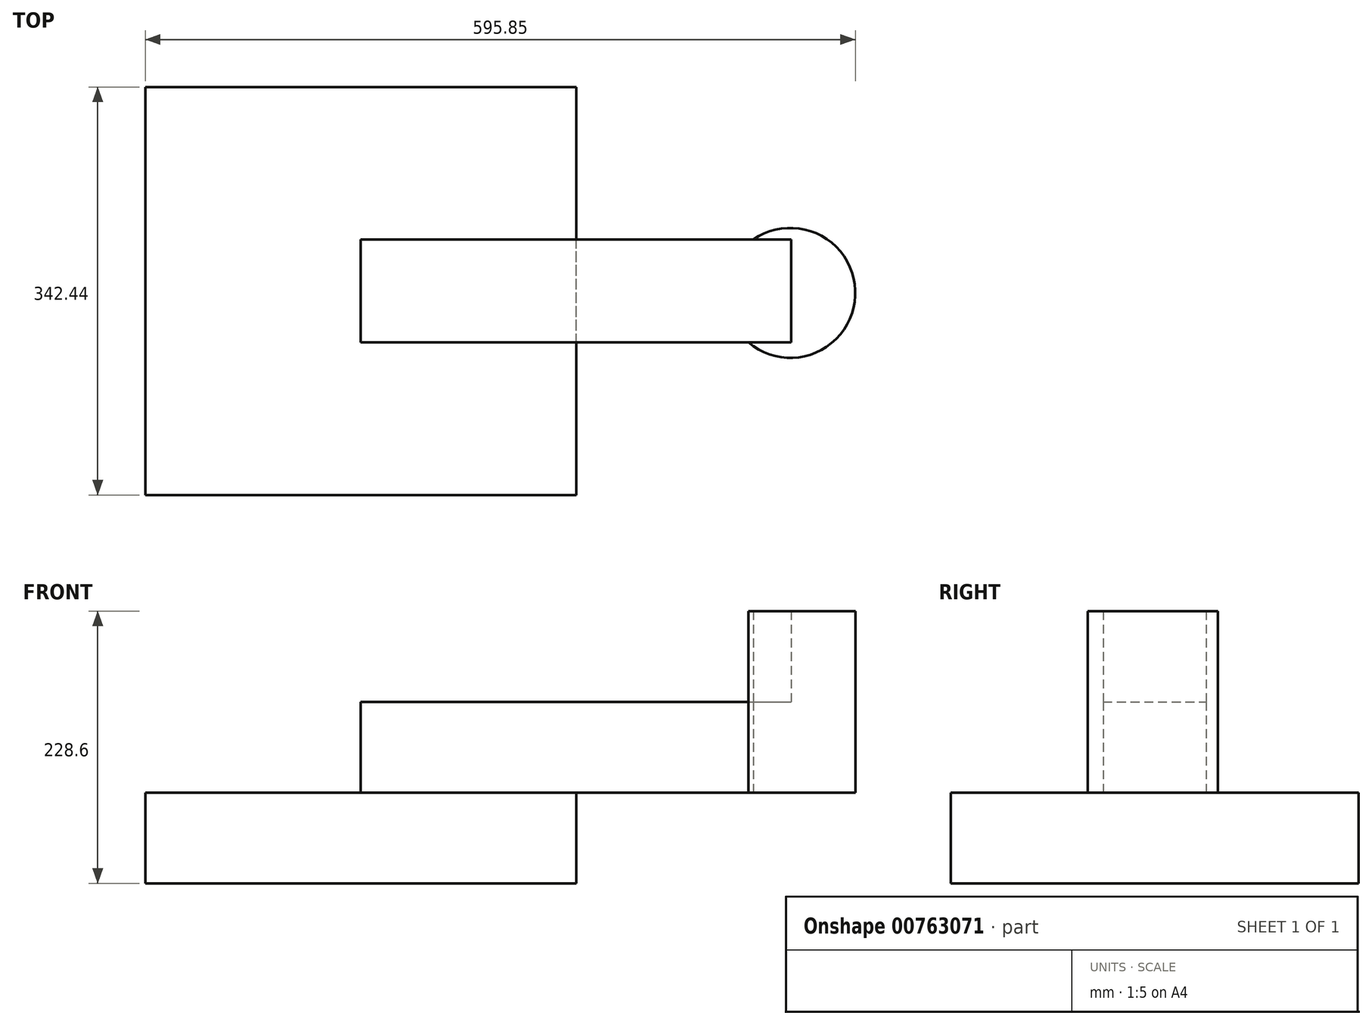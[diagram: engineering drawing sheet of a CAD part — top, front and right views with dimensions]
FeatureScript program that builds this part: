
annotation { "Feature Type Name" : "Feature", "Feature Type Description" : "" }
export const myFeature = defineFeature(function(context is Context, id is Id, definition is map)
    precondition{}
    {
        {
            var Q0;
            Q0=qCreatedBy(makeId("Top.planeOp"),FACE);
            var sketch = newSketch(context, id + "F0", { "sketchPlane" : qUnion([Q0])});
            skLineSegment(sketch, "E0.bottom", {"start": v(180.82, -171.22) * mm, "end": v(-180.82, -171.22) * mm});
            skLineSegment(sketch, "E0.top", {"start": v(180.82, 171.22) * mm, "end": v(-180.82, 171.22) * mm});
            skLineSegment(sketch, "E0.left", {"start": v(180.82, -171.22) * mm, "end": v(180.82, 171.22) * mm});
            skLineSegment(sketch, "E0.right", {"start": v(-180.82, -171.22) * mm, "end": v(-180.82, 171.22) * mm});
            skPoint(sketch, "E0.middle", {"position": v(0, 0) * mm});
            skPoint(sketch, "E1.middle", {"position": v(180.82, 0) * mm});
            skPoint(sketch, "E2.orphan", {"position": v(361.63, 61.98) * mm});
            skPoint(sketch, "E3.orphan", {"position": v(361.63, -61.98) * mm});
            skPoint(sketch, "E4.orphan", {"position": v(0, 61.98) * mm});
            skPoint(sketch, "E1.left.start.orphan", {"position": v(0, -61.98) * mm});
            skSolve(sketch);
        }
        {
            var Q0;
            Q0=qCreatedBy(makeId("Top.planeOp"),FACE);
            var sketch = newSketch(context, id + "F1", { "sketchPlane" : qUnion([Q0])});
            skLineSegment(sketch, "E5.bottom", {"start": v(0, -43.17) * mm, "end": v(361.18, -43.17) * mm});
            skLineSegment(sketch, "E5.top", {"start": v(0, 43.17) * mm, "end": v(361.18, 43.17) * mm});
            skLineSegment(sketch, "E5.left", {"start": v(0, -43.17) * mm, "end": v(0, 43.17) * mm});
            skLineSegment(sketch, "E5.right", {"start": v(361.18, -43.17) * mm, "end": v(361.18, 43.17) * mm});
            skPoint(sketch, "E5.middle", {"position": v(180.6, 0) * mm});
            skSolve(sketch);
        }
        {
            var Q0;
            Q0=makeQuery(id+"F0.imprint","IMPRINT",FACE,{"disambiguationData":[TD([[makeQuery(id+"F0.imprint","IMPRINT",EDGE,{"derivedFrom":sQuery(id+"F0.wireOp",EDGE,"E0.bottom")}),-1.0]])]});
            extrude(context, id + "F2", {"entities" : qUnion([Q0]), "depth" : 76.2 * mm, "offsetDistance" : 25.4 * mm});
        }
        {
            var Q0;
            Q0=makeQuery(id+"F1.imprint","IMPRINT",FACE,{"disambiguationData":[TD([[makeQuery(id+"F1.imprint","IMPRINT",EDGE,{"derivedFrom":sQuery(id+"F1.wireOp",EDGE,"E5.bottom")}),1.0]])]});
            extrude(context, id + "F3", {"entities" : qUnion([Q0]), "operationType" : NewBodyOperationType.ADD, "depth" : 152.4 * mm, "offsetDistance" : 25.4 * mm});
        }
        {
            var Q0;
            Q0=makeQuery(id+"F3.opExtrude","CAP_FACE",FACE,{"disambiguationData":[OSD([sQuery(id+"F1.wireOp",EDGE,"E5.bottom"),sQuery(id+"F1.wireOp",EDGE,"E5.top"),sQuery(id+"F1.wireOp",EDGE,"E5.left"),sQuery(id+"F1.wireOp",EDGE,"E5.right")])],"isStart":false});
            var sketch = newSketch(context, id + "F4", { "sketchPlane" : qUnion([Q0])});
            skCircle(sketch, "E6", {"center": v(360.5, -1.58) * mm, "radius": 54.53 * mm});
            skSolve(sketch);
        }
        {
            var Q0;
            {var subQ5=makeQuery(id+"F3.opExtrude","CAP_EDGE",EDGE,{"disambiguationData":[OSD([sQuery(id+"F1.wireOp",EDGE,"E5.right")])],"isStart":false});Q0=makeQuery(id+"F4.imprint","IMPRINT",FACE,{"disambiguationData":[TD([[makeQuery(id+"F4.imprint","IMPRINT",EDGE,{"derivedFrom":subQ5}),-1.0]])]});}
            extrude(context, id + "F5", {"entities" : qUnion([Q0]), "operationType" : NewBodyOperationType.ADD, "endBound" : BoundingType.SYMMETRIC, "depth" : 152.4 * mm, "offsetDistance" : 25.4 * mm});
        }
        {
            var Q0;
            Q0=makeQuery(id+"F3.opExtrude","SWEPT_FACE",FACE,{"disambiguationData":[OSD([sQuery(id+"F1.wireOp",EDGE,"E5.top")])]});
            var sketch = newSketch(context, id + "F6", { "sketchPlane" : qUnion([Q0])});
            skLineSegment(sketch, "E7.bottom", {"start": v(-361.18, 0) * mm, "end": v(-180.82, 0) * mm});
            skLineSegment(sketch, "E7.top", {"start": v(-361.18, 76.2) * mm, "end": v(-180.82, 76.2) * mm});
            skLineSegment(sketch, "E7.left", {"start": v(-361.18, 0) * mm, "end": v(-361.18, 76.2) * mm});
            skLineSegment(sketch, "E7.right", {"start": v(-180.82, 0) * mm, "end": v(-180.82, 76.2) * mm});
            skSolve(sketch);
        }
        {
            var Q0;
            Q0 = qSketchRegion(id + "F6", true);
            extrude(context, id + "F7", {"entities" : qUnion([Q0]), "operationType" : NewBodyOperationType.REMOVE, "endBound" : BoundingType.THROUGH_ALL, "oppositeDirection" : true, "depth" : 25.4 * mm, "offsetDistance" : 25.4 * mm});
        }
    });
